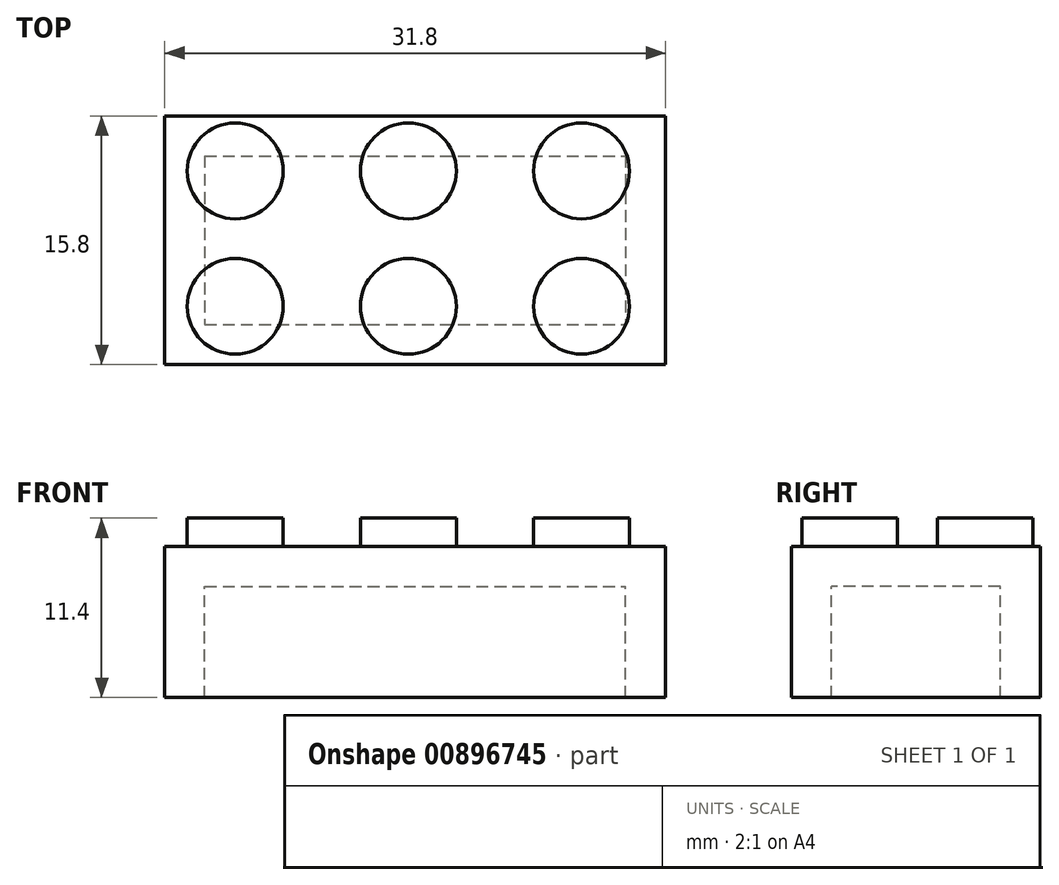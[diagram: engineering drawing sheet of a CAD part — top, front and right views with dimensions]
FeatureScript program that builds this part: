
annotation { "Feature Type Name" : "Feature", "Feature Type Description" : "" }
export const myFeature = defineFeature(function(context is Context, id is Id, definition is map)
    precondition{}
    {
        {
            var Q0;
            Q0=qCreatedBy(makeId("Top.planeOp"),FACE);
            var sketch = newSketch(context, id + "F0", { "sketchPlane" : qUnion([Q0])});
            skLineSegment(sketch, "E0.bottom", {"start": v(-7.46, 11.55) * mm, "end": v(24.34, 11.55) * mm});
            skLineSegment(sketch, "E0.top", {"start": v(-7.46, -4.25) * mm, "end": v(24.34, -4.25) * mm});
            skLineSegment(sketch, "E0.left", {"start": v(-7.46, 11.55) * mm, "end": v(-7.46, -4.25) * mm});
            skLineSegment(sketch, "E0.right", {"start": v(24.34, 11.55) * mm, "end": v(24.34, -4.25) * mm});
            skSolve(sketch);
        }
        {
            var Q0;
            Q0 = qSketchRegion(id + "F0", true);
            extrude(context, id + "F1", {"entities" : qUnion([Q0]), "oppositeDirection" : true, "depth" : 9.6 * mm, "offsetDistance" : 25.4 * mm});
        }
        {
            var Q0;
            Q0=makeQuery(id+"F1.opExtrude","CAP_FACE",FACE,{"disambiguationData":[OSD([sQuery(id+"F0.wireOp",EDGE,"E0.bottom"),sQuery(id+"F0.wireOp",EDGE,"E0.top"),sQuery(id+"F0.wireOp",EDGE,"E0.left"),sQuery(id+"F0.wireOp",EDGE,"E0.right")])],"isStart":false});
            shell(context, id + "F2", {"entities" : qUnion([Q0]), "thickness" : 2.54 * mm});
        }
        {
            var Q0;
            Q0=makeQuery(id+"F1.opExtrude","CAP_FACE",FACE,{"disambiguationData":[OSD([sQuery(id+"F0.wireOp",EDGE,"E0.bottom"),sQuery(id+"F0.wireOp",EDGE,"E0.top"),sQuery(id+"F0.wireOp",EDGE,"E0.left"),sQuery(id+"F0.wireOp",EDGE,"E0.right")])],"isStart":true});
            var sketch = newSketch(context, id + "F3", { "sketchPlane" : qUnion([Q0])});
            skCircle(sketch, "E1", {"center": v(19.01, 8.05) * mm, "radius": 3.04 * mm});
            skCircle(sketch, "E2.0.1.0", {"center": v(19.01, -0.55) * mm, "radius": 3.04 * mm});
            skCircle(sketch, "E2.1.0.0", {"center": v(8.01, 8.05) * mm, "radius": 3.04 * mm});
            skCircle(sketch, "E2.1.1.0", {"center": v(8.01, -0.55) * mm, "radius": 3.04 * mm});
            skCircle(sketch, "E2.2.0.0", {"center": v(-2.99, 8.05) * mm, "radius": 3.04 * mm});
            skCircle(sketch, "E2.2.1.0", {"center": v(-2.99, -0.55) * mm, "radius": 3.04 * mm});
            skLineSegment(sketch, "E2.direction1", {"start": v(19.01, 8.05) * mm, "end": v(8.01, 8.05) * mm, "construction": true});
            skLineSegment(sketch, "E2.direction2", {"start": v(19.01, 8.05) * mm, "end": v(19.01, -0.55) * mm, "construction": true});
            skSolve(sketch);
        }
        {
            var Q0;
            Q0=makeQuery(id+"F3.imprint","IMPRINT",FACE,{"disambiguationData":[TD([[makeQuery(id+"F3.imprint","IMPRINT",EDGE,{"derivedFrom":sQuery(id+"F3.wireOp",EDGE,"E1")}),1.0]])]});
            var Q1;
            Q1=makeQuery(id+"F3.imprint","IMPRINT",FACE,{"disambiguationData":[TD([[makeQuery(id+"F3.imprint","IMPRINT",EDGE,{"derivedFrom":sQuery(id+"F3.wireOp",EDGE,"E2.0.1.0")}),1.0]])]});
            var Q2;
            Q2=makeQuery(id+"F3.imprint","IMPRINT",FACE,{"disambiguationData":[TD([[makeQuery(id+"F3.imprint","IMPRINT",EDGE,{"derivedFrom":sQuery(id+"F3.wireOp",EDGE,"E2.1.0.0")}),1.0]])]});
            var Q3;
            Q3=makeQuery(id+"F3.imprint","IMPRINT",FACE,{"disambiguationData":[TD([[makeQuery(id+"F3.imprint","IMPRINT",EDGE,{"derivedFrom":sQuery(id+"F3.wireOp",EDGE,"E2.1.1.0")}),1.0]])]});
            var Q4;
            Q4=makeQuery(id+"F3.imprint","IMPRINT",FACE,{"disambiguationData":[TD([[makeQuery(id+"F3.imprint","IMPRINT",EDGE,{"derivedFrom":sQuery(id+"F3.wireOp",EDGE,"E2.2.0.0")}),1.0]])]});
            var Q5;
            Q5=makeQuery(id+"F3.imprint","IMPRINT",FACE,{"disambiguationData":[TD([[makeQuery(id+"F3.imprint","IMPRINT",EDGE,{"derivedFrom":sQuery(id+"F3.wireOp",EDGE,"E2.2.1.0")}),1.0]])]});
            extrude(context, id + "F4", {"entities" : qUnion([Q0, Q1, Q2, Q3, Q4, Q5]), "operationType" : NewBodyOperationType.ADD, "depth" : 1.8 * mm, "offsetDistance" : 25 * mm});
        }
    });
